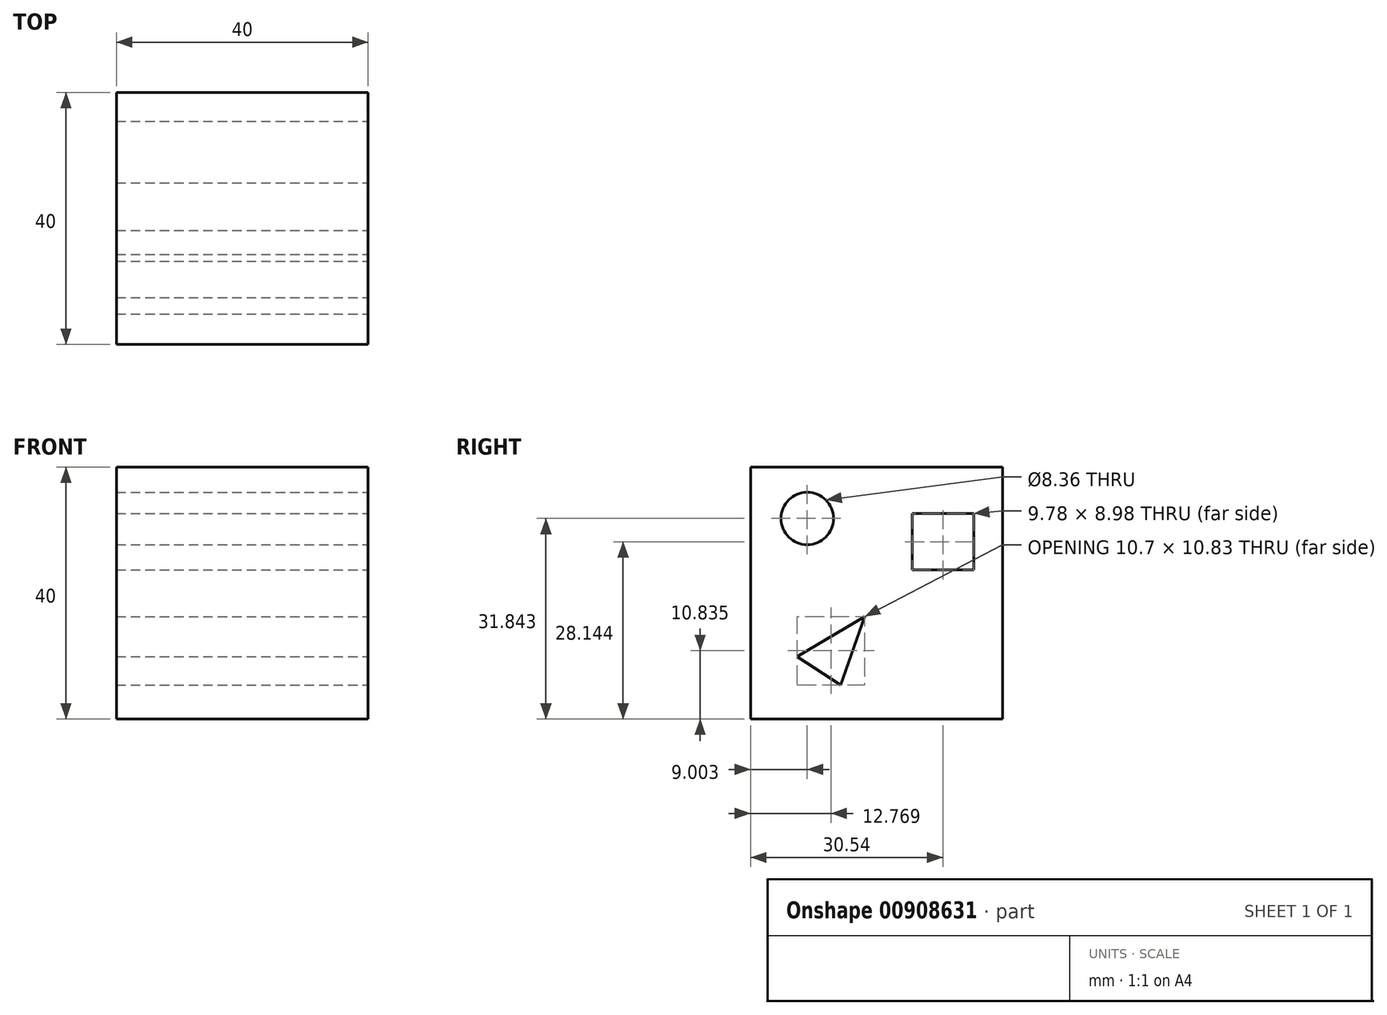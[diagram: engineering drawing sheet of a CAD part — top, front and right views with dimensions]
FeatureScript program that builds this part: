
annotation { "Feature Type Name" : "Feature", "Feature Type Description" : "" }
export const myFeature = defineFeature(function(context is Context, id is Id, definition is map)
    precondition{}
    {
        {
            var Q0;
            Q0=qCreatedBy(makeId("Top.planeOp"),FACE);
            var sketch = newSketch(context, id + "F0", { "sketchPlane" : qUnion([Q0])});
            skLineSegment(sketch, "E0.bottom", {"start": v(-21.32, 21.88) * mm, "end": v(18.68, 21.88) * mm});
            skLineSegment(sketch, "E0.top", {"start": v(-21.32, -18.12) * mm, "end": v(18.68, -18.12) * mm});
            skLineSegment(sketch, "E0.left", {"start": v(-21.32, 21.88) * mm, "end": v(-21.32, -18.12) * mm});
            skLineSegment(sketch, "E0.right", {"start": v(18.68, 21.88) * mm, "end": v(18.68, -18.12) * mm});
            skSolve(sketch);
        }
        {
            var Q0;
            Q0 = qSketchRegion(id + "F0", true);
            extrude(context, id + "F1", {"entities" : qUnion([Q0]), "depth" : 25 * mm, "offsetDistance" : 25 * mm});
        }
        {
            var Q0;
            Q0 = qSketchRegion(id + "F0", true);
            extrude(context, id + "F2", {"entities" : qUnion([Q0]), "operationType" : NewBodyOperationType.ADD, "depth" : 40 * mm, "offsetDistance" : 25 * mm});
        }
        {
            var Q0;
            {var subQ0=sQuery(id+"F0.wireOp",EDGE,"E0.right");Q0=makeQuery(id+"F2.boolean.opBoolean","MERGE",FACE,{"derivedFrom":[makeQuery(id+"F1.opExtrude","SWEPT_FACE",FACE,{"disambiguationData":[OSD([subQ0])]}),makeQuery(id+"F2.opExtrude","SWEPT_FACE",FACE,{"disambiguationData":[OSD([subQ0])]})]});}
            var sketch = newSketch(context, id + "F3", { "sketchPlane" : qUnion([Q0])});
            skCircle(sketch, "E1", {"center": v(-9.12, 31.84) * mm, "radius": 4.18 * mm});
            skLineSegment(sketch, "E2.bottom", {"start": v(7.53, 32.64) * mm, "end": v(17.3, 32.64) * mm});
            skLineSegment(sketch, "E2.top", {"start": v(7.53, 23.65) * mm, "end": v(17.3, 23.65) * mm});
            skLineSegment(sketch, "E2.left", {"start": v(7.53, 32.64) * mm, "end": v(7.53, 23.65) * mm});
            skLineSegment(sketch, "E2.right", {"start": v(17.3, 32.64) * mm, "end": v(17.3, 23.65) * mm});
            skLineSegment(sketch, "E3", {"start": v(-10.7, 9.9) * mm, "end": v(-3.83, 5.42) * mm});
            skLineSegment(sketch, "E4", {"start": v(-10.7, 9.9) * mm, "end": v(0, 16.25) * mm});
            skLineSegment(sketch, "E5", {"start": v(0, 16.25) * mm, "end": v(-3.83, 5.42) * mm});
            skSolve(sketch);
        }
        {
            var Q0;
            Q0 = qSketchRegion(id + "F3", true);
            extrude(context, id + "F4", {"entities" : qUnion([Q0]), "operationType" : NewBodyOperationType.REMOVE, "endBound" : BoundingType.THROUGH_ALL, "oppositeDirection" : true, "depth" : 25 * mm, "offsetDistance" : 25 * mm});
        }
    });
